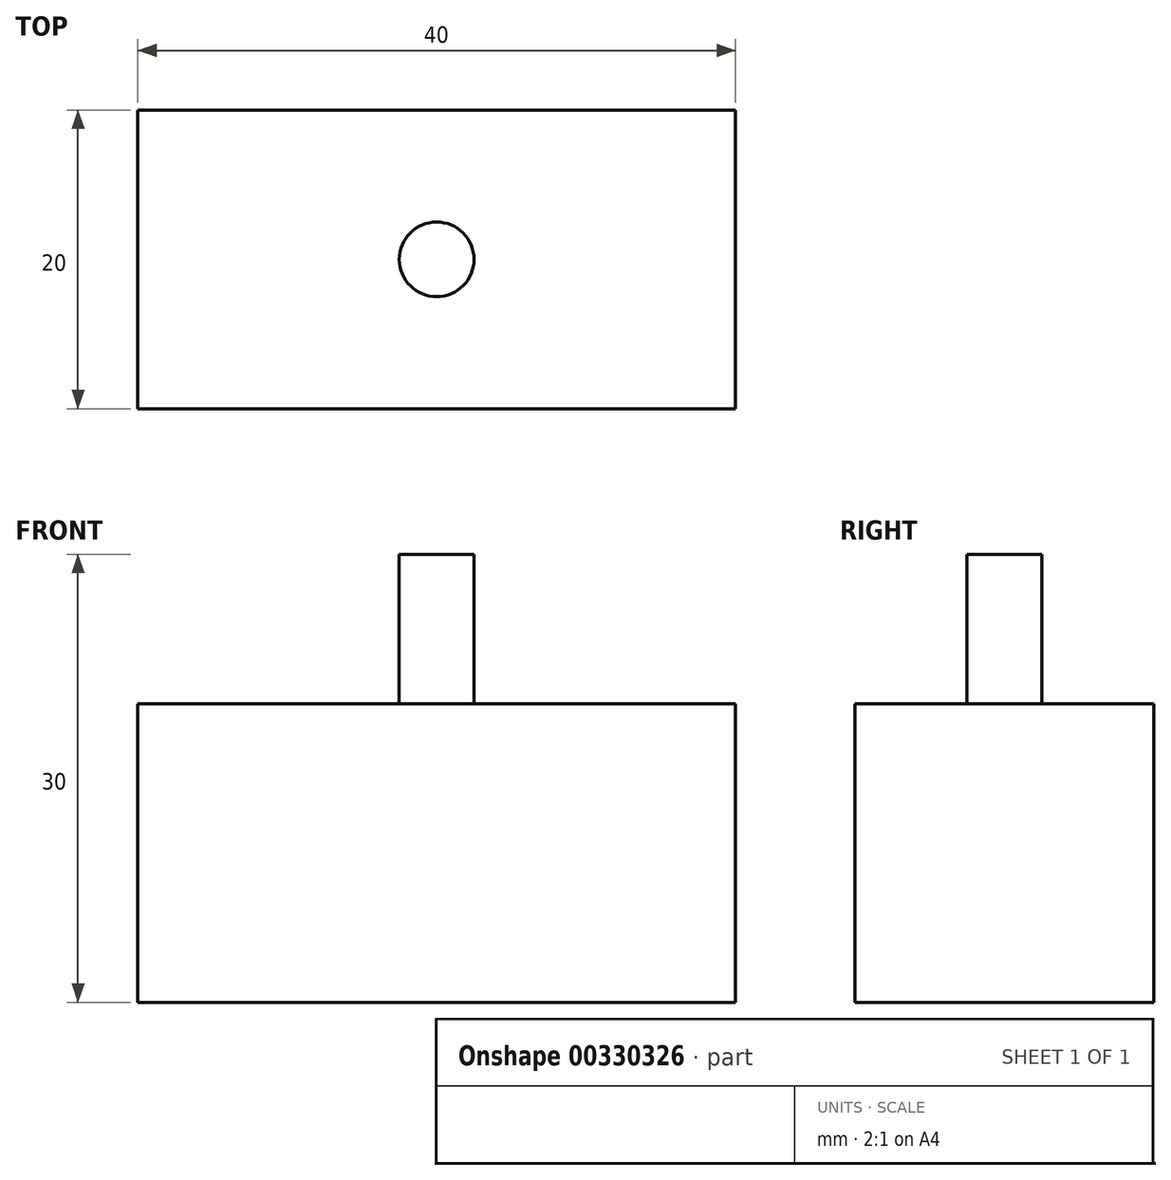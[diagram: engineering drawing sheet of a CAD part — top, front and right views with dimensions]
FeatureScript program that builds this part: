
annotation { "Feature Type Name" : "Feature", "Feature Type Description" : "" }
export const myFeature = defineFeature(function(context is Context, id is Id, definition is map)
    precondition{}
    {
        {
            var Q0;
            Q0=qCreatedBy(makeId("Front.planeOp"),FACE);
            var sketch = newSketch(context, id + "F0", { "sketchPlane" : qUnion([Q0])});
            skLineSegment(sketch, "E0.bottom", {"start": v(-21.67, -5.22) * mm, "end": v(18.33, -5.22) * mm});
            skLineSegment(sketch, "E0.top", {"start": v(-21.67, -25.22) * mm, "end": v(18.33, -25.22) * mm});
            skLineSegment(sketch, "E0.left", {"start": v(-21.67, -5.22) * mm, "end": v(-21.67, -25.22) * mm});
            skLineSegment(sketch, "E0.right", {"start": v(18.33, -5.22) * mm, "end": v(18.33, -25.22) * mm});
            skSolve(sketch);
        }
        {
            var Q0;
            Q0 = qSketchRegion(id + "F0", true);
            extrude(context, id + "F1", {"entities" : qUnion([Q0]), "depth" : 20 * mm});
        }
        {
            var Q0;
            Q0=makeQuery(id+"F1.opExtrude","SWEPT_FACE",FACE,{"disambiguationData":[OSD([sQuery(id+"F0.wireOp",EDGE,"E0.bottom")])]});
            var sketch = newSketch(context, id + "F2", { "sketchPlane" : qUnion([Q0])});
            skLineSegment(sketch, "E1", {"start": v(-1.67, 0) * mm, "end": v(-1.67, -20) * mm, "construction": true});
            skLineSegment(sketch, "E2", {"start": v(-21.67, -10) * mm, "end": v(18.33, -10) * mm, "construction": true});
            skCircle(sketch, "E3", {"center": v(-1.67, -10) * mm, "radius": 2.5 * mm});
            skSolve(sketch);
        }
        {
            var Q0;
            Q0 = qSketchRegion(id + "F2", true);
            extrude(context, id + "F3", {"entities" : qUnion([Q0]), "operationType" : NewBodyOperationType.ADD, "depth" : 10 * mm});
        }
    });
